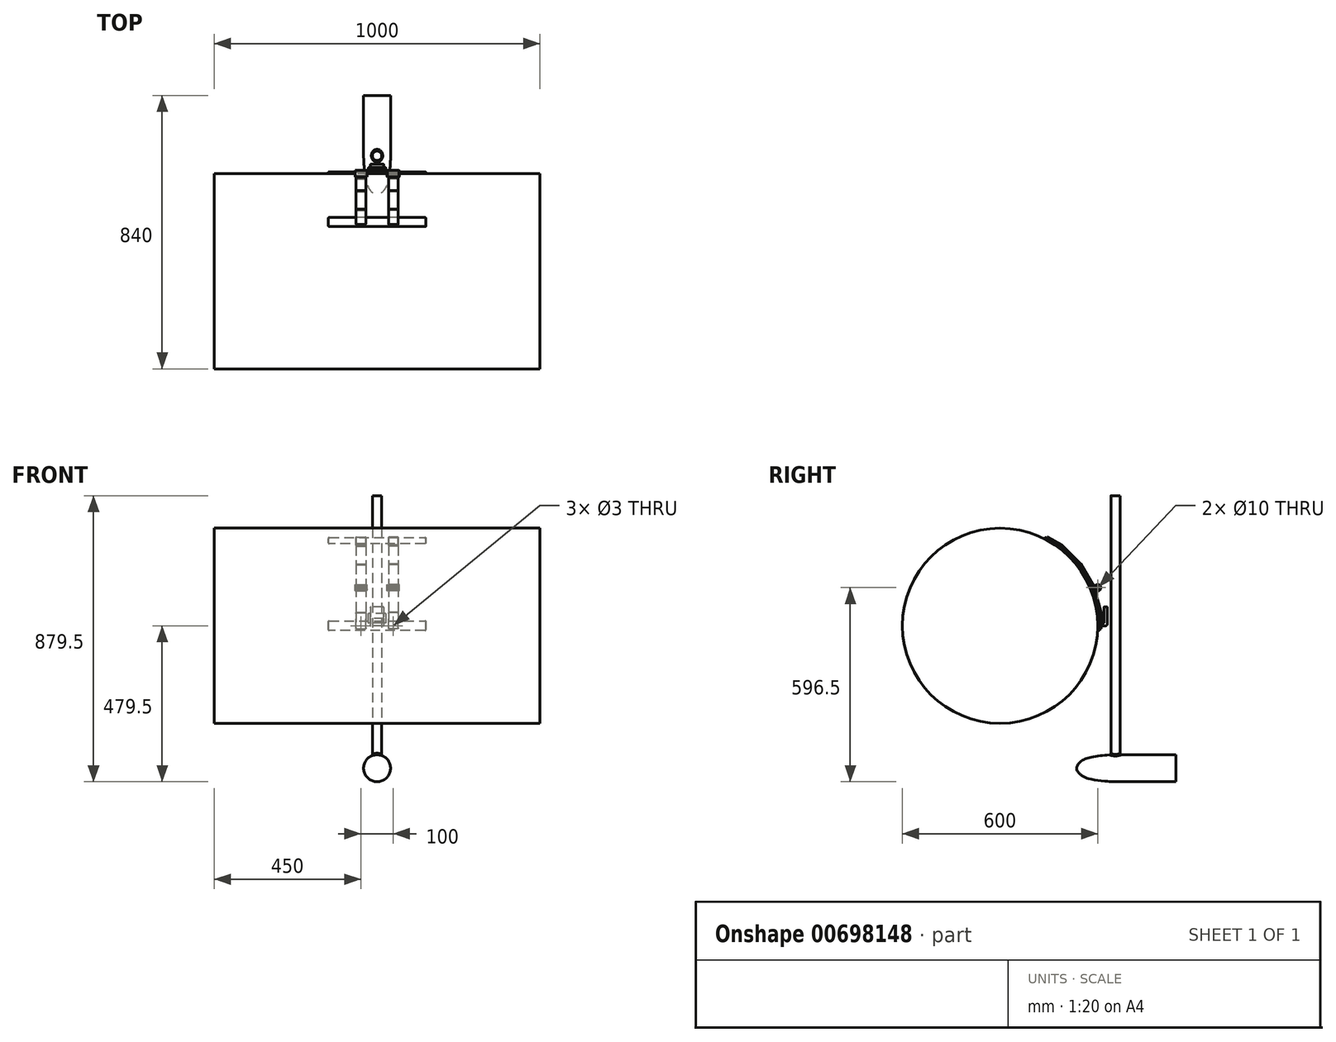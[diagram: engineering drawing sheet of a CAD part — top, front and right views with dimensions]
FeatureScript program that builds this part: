
annotation { "Feature Type Name" : "Feature", "Feature Type Description" : "" }
export const myFeature = defineFeature(function(context is Context, id is Id, definition is map)
    precondition{}
    {
        {
            var Q0;
            Q0=qCreatedBy(makeId("Right.planeOp"),FACE);
            var sketch = newSketch(context, id + "F0", { "sketchPlane" : qUnion([Q0])});
            skCircle(sketch, "E0", {"center": v(0, 0) * mm, "radius": 300 * mm});
            skSolve(sketch);
        }
        {
            var Q0;
            Q0=makeQuery(id+"F0.imprint","IMPRINT",FACE,{"disambiguationData":[TD([[makeQuery(id+"F0.imprint","IMPRINT",EDGE,{"derivedFrom":sQuery(id+"F0.wireOp",EDGE,"E0")}),1.0]])]});
            extrude(context, id + "F1", {"entities" : qUnion([Q0]), "endBound" : BoundingType.SYMMETRIC, "depth" : 1000 * mm, "offsetDistance" : 25 * mm});
        }
        {
            var Q0;
            Q0=qCreatedBy(makeId("Top.planeOp"),FACE);
            var sketch = newSketch(context, id + "F2", { "sketchPlane" : qUnion([Q0])});
            skLineSegment(sketch, "E1", {"start": v(0, 0) * mm, "end": v(0, 431.37) * mm, "construction": true});
            skCircle(sketch, "E2", {"center": v(0, 355) * mm, "radius": 14.5 * mm});
            skSolve(sketch);
        }
        {
            var Q0;
            Q0=makeQuery(id+"F2.imprint","IMPRINT",FACE,{"disambiguationData":[TD([[makeQuery(id+"F2.imprint","IMPRINT",EDGE,{"derivedFrom":sQuery(id+"F2.wireOp",EDGE,"E2")}),1.0]])]});
            extrude(context, id + "F3", {"entities" : qUnion([Q0]), "endBound" : BoundingType.SYMMETRIC, "depth" : 800 * mm, "offsetDistance" : 25 * mm});
        }
        {
            var Q0;
            Q0=qCreatedBy(makeId("Right.planeOp"),FACE);
            var sketch = newSketch(context, id + "F4", { "sketchPlane" : qUnion([Q0])});
            skLineSegment(sketch, "E3", {"start": v(235, -396.5) * mm, "end": v(384.53, -396.5) * mm, "construction": true});
            skLineSegment(sketch, "E4", {"start": v(355, -389.88) * mm, "end": v(355, -511.75) * mm, "construction": true});
            skFitSpline(sketch, "E5", {"points": [v(355, -396.5) * mm, v(273.73, -405.4) * mm, v(244.54, -420.82) * mm, v(235.02, -438) * mm], "startDerivative": vector(-142.28, 0) * mm, "endDerivative": vector(-0.8, -75.3) * mm});
            skLineSegment(sketch, "E6", {"start": v(355, -396.5) * mm, "end": v(540, -396.5) * mm});
            skLineSegment(sketch, "E7", {"start": v(540, -396.5) * mm, "end": v(540, -438) * mm});
            skLineSegment(sketch, "E8", {"start": v(235.02, -438) * mm, "end": v(540, -438) * mm});
            skSolve(sketch);
        }
        {
            var Q0;
            Q0 = qSketchRegion(id + "F4", true);
            var Q1;
            Q1=sQuery(id+"F4.wireOp",EDGE,"E8");
            revolve(context, id + "F5", {"surfaceOperationType" : NewSurfaceOperationType.NEW, "entities" : qUnion([Q0]), "axis" : qUnion([Q1]), "revolveType" : RevolveType.FULL});
        }
        {
            var Q0;
            Q0=sQuery(id+"F0.wireOp",EDGE,"E0");
            extrude(context, id + "F6", {"bodyType" : ToolBodyType.SURFACE, "surfaceEntities" : qUnion([Q0]), "endBound" : BoundingType.SYMMETRIC, "depth" : 1000 * mm, "offsetDistance" : 25 * mm});
        }
        {
            var Q0;
            Q0=makeQuery(id+"F3.opExtrude","SWEPT_BODY",BODY,{"disambiguationData":[OSD([sQuery(id+"F2.wireOp",EDGE,"E2")])]});
            var Q1;
            Q1=makeQuery(id+"F5.opRevolve","SWEPT_BODY",BODY,{"disambiguationData":[OSD([sQuery(id+"F4.wireOp",EDGE,"E5"),sQuery(id+"F4.wireOp",EDGE,"E6"),sQuery(id+"F4.wireOp",EDGE,"E7"),sQuery(id+"F4.wireOp",EDGE,"iDBx6k7e-QWYk-5wCq-wD4t-SSnstJS5jygN")])]});
            booleanBodies(context, id + "F7", {"operationType" : BooleanOperationType.UNION, "tools" : qUnion([Q0, Q1])});
        }
        {
            var Q0;
            Q0=makeQuery(id+"F7.opBoolean","INTERSECT",EDGE,{"derivedFrom":[makeQuery(id+"F3.opExtrude","SWEPT_FACE",FACE,{"disambiguationData":[OSD([sQuery(id+"F2.wireOp",EDGE,"E2")])]}),makeQuery(id+"F5.opRevolve","SWEPT_FACE",FACE,{"disambiguationData":[OSD([sQuery(id+"F4.wireOp",EDGE,"E6")])]})]});
            fillet(context, id + "F8", {"entities" : qUnion([Q0]), "radius" : 5 * mm, "tangentPropagation" : true, "allowEdgeOverflow" : false});
        }
        {
            var Q0;
            Q0=qCreatedBy(makeId("Right.planeOp"),FACE);
            cPlane(context, id + "F9", {"entities" : qUnion([Q0]), "cplaneType" : CPlaneType.OFFSET, "offset" : 35 * mm, "width" : 150 * mm, "height" : 150 * mm});
        }
        {
            var Q0;
            Q0=qCreatedBy(makeId("Right.planeOp"),FACE);
            var sketch = newSketch(context, id + "F10", { "sketchPlane" : qUnion([Q0])});
            skLineSegment(sketch, "E9", {"start": v(0, 0) * mm, "end": v(152.5, 264.14) * mm, "construction": true});
            skLineSegment(sketch, "E10", {"start": v(152.5, 264.14) * mm, "end": v(165.5, 256.64) * mm});
            skLineSegment(sketch, "E11", {"start": v(163, 252.3) * mm, "end": v(137, 267.3) * mm});
            skLineSegment(sketch, "E12", {"start": v(152.5, 264.14) * mm, "end": v(139.42, 271.7) * mm});
            skLineSegment(sketch, "E13", {"start": v(139.42, 271.7) * mm, "end": v(137, 267.3) * mm});
            skLineSegment(sketch, "E14", {"start": v(165.5, 256.64) * mm, "end": v(163, 252.3) * mm});
            skSolve(sketch);
        }
        {
            var Q0;
            Q0 = qSketchRegion(id + "F10", true);
            extrude(context, id + "F11", {"entities" : qUnion([Q0]), "endBound" : BoundingType.SYMMETRIC, "depth" : 300 * mm, "offsetDistance" : 25 * mm});
        }
        {
            var Q0;
            Q0=makeQuery(id+"F11.opExtrude","CAP_EDGE",EDGE,{"disambiguationData":[OSD([sQuery(id+"F10.wireOp",EDGE,"E11")])],"isStart":false});
            var Q1;
            Q1=makeQuery(id+"F11.opExtrude","CAP_EDGE",EDGE,{"disambiguationData":[OSD([sQuery(id+"F10.wireOp",EDGE,"E10"),sQuery(id+"F10.wireOp",EDGE,"E12")])],"isStart":false});
            var Q2;
            Q2=makeQuery(id+"F11.opExtrude","SWEPT_EDGE",EDGE,{"disambiguationData":[OSD([sQuery(id+"F10.wireOp",EDGE,"E11"),sQuery(id+"F10.wireOp",EDGE,"E13")])]});
            var Q3;
            Q3=makeQuery(id+"F11.opExtrude","SWEPT_EDGE",EDGE,{"disambiguationData":[OSD([sQuery(id+"F10.wireOp",EDGE,"E12"),sQuery(id+"F10.wireOp",EDGE,"E13")])]});
            var Q4;
            Q4=makeQuery(id+"F11.opExtrude","CAP_EDGE",EDGE,{"disambiguationData":[OSD([sQuery(id+"F10.wireOp",EDGE,"E11")])],"isStart":true});
            var Q5;
            Q5=makeQuery(id+"F11.opExtrude","CAP_EDGE",EDGE,{"disambiguationData":[OSD([sQuery(id+"F10.wireOp",EDGE,"E10"),sQuery(id+"F10.wireOp",EDGE,"E12")])],"isStart":true});
            var Q6;
            Q6=makeQuery(id+"F11.opExtrude","SWEPT_EDGE",EDGE,{"disambiguationData":[OSD([sQuery(id+"F10.wireOp",EDGE,"E11"),sQuery(id+"F10.wireOp",EDGE,"E14")])]});
            var Q7;
            Q7=makeQuery(id+"F11.opExtrude","SWEPT_EDGE",EDGE,{"disambiguationData":[OSD([sQuery(id+"F10.wireOp",EDGE,"E10"),sQuery(id+"F10.wireOp",EDGE,"E14")])]});
            fillet(context, id + "F12", {"entities" : qUnion([Q0, Q1, Q2, Q3, Q4, Q5, Q6, Q7]), "tangentPropagation" : true, "radius" : 1 * mm, "defaultsChanged" : false, "vertexSettings" : [], "allowEdgeOverflow" : false});
        }
        {
            var Q0;
            Q0=makeQuery(id+"F11.opExtrude","CAP_EDGE",EDGE,{"disambiguationData":[OSD([sQuery(id+"F10.wireOp",EDGE,"E13")])],"isStart":false});
            var Q1;
            Q1=makeQuery(id+"F11.opExtrude","CAP_EDGE",EDGE,{"disambiguationData":[OSD([sQuery(id+"F10.wireOp",EDGE,"E14")])],"isStart":false});
            var Q2;
            Q2=makeQuery(id+"F11.opExtrude","CAP_EDGE",EDGE,{"disambiguationData":[OSD([sQuery(id+"F10.wireOp",EDGE,"E14")])],"isStart":true});
            var Q3;
            Q3=makeQuery(id+"F11.opExtrude","CAP_EDGE",EDGE,{"disambiguationData":[OSD([sQuery(id+"F10.wireOp",EDGE,"E13")])],"isStart":true});
            fillet(context, id + "F13", {"entities" : qUnion([Q0, Q1, Q2, Q3]), "tangentPropagation" : true, "radius" : 3 * mm, "defaultsChanged" : true, "vertexSettings" : [], "allowEdgeOverflow" : false});
        }
        {
            var Q0;
            Q0=makeQuery(id+"F11.opExtrude","SWEPT_BODY",BODY,{"disambiguationData":[OSD([sQuery(id+"F10.wireOp",EDGE,"E10"),sQuery(id+"F10.wireOp",EDGE,"E11"),sQuery(id+"F10.wireOp",EDGE,"E12"),sQuery(id+"F10.wireOp",EDGE,"E13"),sQuery(id+"F10.wireOp",EDGE,"E14")])]});
            var Q1;
            Q1=makeQuery(id+"F1.opExtrude","SWEPT_FACE",FACE,{"disambiguationData":[OSD([sQuery(id+"F0.wireOp",EDGE,"E0")])]});
            transform(context, id + "F14", {"entities" : qUnion([Q0]), "transformType" : TransformType.ROTATION, "transformAxis" : qUnion([Q1]), "angle" : 60 * degree, "makeCopy" : true});
        }
        {
            var Q0;
            Q0=qCreatedBy(id+"F9.planeOp",FACE);
            var sketch = newSketch(context, id + "F15", { "sketchPlane" : qUnion([Q0])});
            skLineSegment(sketch, "E15", {"start": v(0, 0) * mm, "end": v(165.42, 286.52) * mm, "construction": true});
            skLineSegment(sketch, "E16", {"start": v(0, 0) * mm, "end": v(327, 0) * mm, "construction": true});
            skLineSegment(sketch, "E17", {"start": v(0, 0) * mm, "end": v(202.83, 264.33) * mm, "construction": true});
            skLineSegment(sketch, "E18", {"start": v(0, 0) * mm, "end": v(263.06, 201.85) * mm, "construction": true});
            skLineSegment(sketch, "E19", {"start": v(0, 0) * mm, "end": v(296.71, 122.9) * mm, "construction": true});
            skLineSegment(sketch, "E20", {"start": v(0, 0) * mm, "end": v(324.75, 42.75) * mm, "construction": true});
            skLineSegment(sketch, "E21", {"start": v(143.84, 269.14) * mm, "end": v(187.27, 244.06) * mm});
            skLineSegment(sketch, "E22", {"start": v(190.34, 248.06) * mm, "end": v(146.34, 273.47) * mm});
            skLineSegment(sketch, "E23", {"start": v(146.34, 273.47) * mm, "end": v(143.84, 269.14) * mm});
            skArc(sketch, "E24", {"start": v(187.27, 244.06) * mm, "mid": v(266.42, 153.82) * mm, "end": v(305, 40.15) * mm, "construction": true});
            skLineSegment(sketch, "E25", {"start": v(187.27, 244.06) * mm, "end": v(244.06, 187.27) * mm});
            skLineSegment(sketch, "E26", {"start": v(244.06, 187.27) * mm, "end": v(284.21, 117.73) * mm});
            skLineSegment(sketch, "E27", {"start": v(284.21, 117.73) * mm, "end": v(305, 40.15) * mm});
            skLineSegment(sketch, "E28", {"start": v(305, -10) * mm, "end": v(310, -10) * mm});
            skLineSegment(sketch, "E29", {"start": v(305, 40.15) * mm, "end": v(305, -10) * mm});
            skLineSegment(sketch, "E30", {"start": v(310, -10) * mm, "end": v(310, 40.81) * mm});
            skLineSegment(sketch, "E31", {"start": v(190.34, 248.06) * mm, "end": v(248.06, 190.34) * mm});
            skLineSegment(sketch, "E32", {"start": v(248.06, 190.34) * mm, "end": v(288.87, 119.66) * mm});
            skLineSegment(sketch, "E33", {"start": v(288.87, 119.66) * mm, "end": v(310, 40.81) * mm});
            skSolve(sketch);
        }
        {
            var Q0;
            Q0 = qSketchRegion(id + "F15", true);
            extrude(context, id + "F16", {"entities" : qUnion([Q0]), "depth" : 30 * mm, "offsetDistance" : 25 * mm, "hasSecondDirection" : true, "secondDirectionOppositeDirection" : false, "secondDirectionDepth" : 0 * mm});
        }
        {
            var Q0;
            Q0=makeQuery(id+"F16.opExtrude","CAP_EDGE",EDGE,{"disambiguationData":[OSD([sQuery(id+"F15.wireOp",EDGE,"E22")])],"isStart":false});
            var Q1;
            Q1=makeQuery(id+"F16.opExtrude","CAP_EDGE",EDGE,{"disambiguationData":[OSD([sQuery(id+"F15.wireOp",EDGE,"E21")])],"isStart":false});
            var Q2;
            Q2=makeQuery(id+"F16.opExtrude","CAP_EDGE",EDGE,{"disambiguationData":[OSD([sQuery(id+"F15.wireOp",EDGE,"E22")])],"isStart":true});
            var Q3;
            Q3=makeQuery(id+"F16.opExtrude","CAP_EDGE",EDGE,{"disambiguationData":[OSD([sQuery(id+"F15.wireOp",EDGE,"E21")])],"isStart":true});
            var Q4;
            Q4=makeQuery(id+"F16.opExtrude","CAP_EDGE",EDGE,{"disambiguationData":[OSD([sQuery(id+"F15.wireOp",EDGE,"E31")])],"isStart":false});
            var Q5;
            Q5=makeQuery(id+"F16.opExtrude","CAP_EDGE",EDGE,{"disambiguationData":[OSD([sQuery(id+"F15.wireOp",EDGE,"E32")])],"isStart":false});
            var Q6;
            Q6=makeQuery(id+"F16.opExtrude","CAP_EDGE",EDGE,{"disambiguationData":[OSD([sQuery(id+"F15.wireOp",EDGE,"E33")])],"isStart":false});
            var Q7;
            Q7=makeQuery(id+"F16.opExtrude","CAP_EDGE",EDGE,{"disambiguationData":[OSD([sQuery(id+"F15.wireOp",EDGE,"E27")])],"isStart":false});
            var Q8;
            Q8=makeQuery(id+"F16.opExtrude","CAP_EDGE",EDGE,{"disambiguationData":[OSD([sQuery(id+"F15.wireOp",EDGE,"E30")])],"isStart":false});
            var Q9;
            Q9=makeQuery(id+"F16.opExtrude","CAP_EDGE",EDGE,{"disambiguationData":[OSD([sQuery(id+"F15.wireOp",EDGE,"E29")])],"isStart":false});
            var Q10;
            Q10=makeQuery(id+"F16.opExtrude","SWEPT_EDGE",EDGE,{"disambiguationData":[OSD([sQuery(id+"F15.wireOp",EDGE,"E28"),sQuery(id+"F15.wireOp",EDGE,"E30")])]});
            var Q11;
            Q11=makeQuery(id+"F16.opExtrude","SWEPT_EDGE",EDGE,{"disambiguationData":[OSD([sQuery(id+"F15.wireOp",EDGE,"E28"),sQuery(id+"F15.wireOp",EDGE,"E29")])]});
            var Q12;
            Q12=makeQuery(id+"F16.opExtrude","CAP_EDGE",EDGE,{"disambiguationData":[OSD([sQuery(id+"F15.wireOp",EDGE,"E30")])],"isStart":true});
            var Q13;
            Q13=makeQuery(id+"F16.opExtrude","CAP_EDGE",EDGE,{"disambiguationData":[OSD([sQuery(id+"F15.wireOp",EDGE,"E29")])],"isStart":true});
            var Q14;
            Q14=makeQuery(id+"F16.opExtrude","CAP_EDGE",EDGE,{"disambiguationData":[OSD([sQuery(id+"F15.wireOp",EDGE,"E33")])],"isStart":true});
            var Q15;
            Q15=makeQuery(id+"F16.opExtrude","CAP_EDGE",EDGE,{"disambiguationData":[OSD([sQuery(id+"F15.wireOp",EDGE,"E27")])],"isStart":true});
            var Q16;
            Q16=makeQuery(id+"F16.opExtrude","CAP_EDGE",EDGE,{"disambiguationData":[OSD([sQuery(id+"F15.wireOp",EDGE,"E32")])],"isStart":true});
            var Q17;
            Q17=makeQuery(id+"F16.opExtrude","CAP_EDGE",EDGE,{"disambiguationData":[OSD([sQuery(id+"F15.wireOp",EDGE,"E31")])],"isStart":true});
            var Q18;
            Q18=makeQuery(id+"F16.opExtrude","CAP_EDGE",EDGE,{"disambiguationData":[OSD([sQuery(id+"F15.wireOp",EDGE,"E26")])],"isStart":true});
            var Q19;
            Q19=makeQuery(id+"F16.opExtrude","CAP_EDGE",EDGE,{"disambiguationData":[OSD([sQuery(id+"F15.wireOp",EDGE,"E25")])],"isStart":true});
            var Q20;
            Q20=makeQuery(id+"F16.opExtrude","SWEPT_EDGE",EDGE,{"disambiguationData":[OSD([sQuery(id+"F15.wireOp",EDGE,"E22"),sQuery(id+"F15.wireOp",EDGE,"E23")])]});
            var Q21;
            Q21=makeQuery(id+"F16.opExtrude","CAP_EDGE",EDGE,{"disambiguationData":[OSD([sQuery(id+"F15.wireOp",EDGE,"E26")])],"isStart":false});
            var Q22;
            Q22=makeQuery(id+"F16.opExtrude","CAP_EDGE",EDGE,{"disambiguationData":[OSD([sQuery(id+"F15.wireOp",EDGE,"E25")])],"isStart":false});
            var Q23;
            Q23=makeQuery(id+"F16.opExtrude","SWEPT_EDGE",EDGE,{"disambiguationData":[OSD([sQuery(id+"F15.wireOp",EDGE,"E21"),sQuery(id+"F15.wireOp",EDGE,"E23")])]});
            var Q24;
            Q24=makeQuery(id+"F16.opExtrude","CAP_EDGE",EDGE,{"disambiguationData":[OSD([sQuery(id+"F15.wireOp",EDGE,"E23")])],"isStart":true});
            var Q25;
            Q25=makeQuery(id+"F16.opExtrude","CAP_EDGE",EDGE,{"disambiguationData":[OSD([sQuery(id+"F15.wireOp",EDGE,"E23")])],"isStart":false});
            var Q26;
            Q26=makeQuery(id+"F16.opExtrude","CAP_EDGE",EDGE,{"disambiguationData":[OSD([sQuery(id+"F15.wireOp",EDGE,"E28")])],"isStart":true});
            var Q27;
            Q27=makeQuery(id+"F16.opExtrude","CAP_EDGE",EDGE,{"disambiguationData":[OSD([sQuery(id+"F15.wireOp",EDGE,"E28")])],"isStart":false});
            fillet(context, id + "F17", {"entities" : qUnion([Q0, Q1, Q2, Q3, Q4, Q5, Q6, Q7, Q8, Q9, Q10, Q11, Q12, Q13, Q14, Q15, Q16, Q17, Q18, Q19, Q20, Q21, Q22, Q23, Q24, Q25, Q26, Q27]), "tangentPropagation" : true, "radius" : 1 * mm, "defaultsChanged" : false, "vertexSettings" : [], "allowEdgeOverflow" : false});
        }
        {
            var Q0;
            Q0=qCreatedBy(makeId("Right.planeOp"),FACE);
            var sketch = newSketch(context, id + "F18", { "sketchPlane" : qUnion([Q0])});
            skCircle(sketch, "E34", {"center": v(300, 117) * mm, "radius": 10 * mm});
            skCircle(sketch, "E35", {"center": v(300, 117) * mm, "radius": 5 * mm});
            skLineSegment(sketch, "E36", {"start": v(311, 8) * mm, "end": v(319, 8) * mm});
            skLineSegment(sketch, "E37", {"start": v(319, 8) * mm, "end": v(319, 38) * mm});
            skLineSegment(sketch, "E38", {"start": v(319, 38) * mm, "end": v(311, 38) * mm});
            skLineSegment(sketch, "E39", {"start": v(311, 38) * mm, "end": v(311, 8) * mm});
            skSolve(sketch);
        }
        {
            var Q0;
            Q0=makeQuery(id+"F18.imprint","IMPRINT",FACE,{"disambiguationData":[TD([[makeQuery(id+"F18.imprint","IMPRINT",EDGE,{"derivedFrom":sQuery(id+"F18.wireOp",EDGE,"E34")}),1.0]])]});
            extrude(context, id + "F19", {"entities" : qUnion([Q0]), "depth" : 68 * mm, "offsetDistance" : 25 * mm, "hasSecondDirection" : true, "secondDirectionOppositeDirection" : false, "secondDirectionDepth" : 30 * mm});
        }
        {
            var Q0;
            Q0=makeQuery(id+"F19.opExtrude","CAP_EDGE",EDGE,{"disambiguationData":[OSD([sQuery(id+"F18.wireOp",EDGE,"E35")])],"isStart":false});
            var Q1;
            Q1=makeQuery(id+"F19.opExtrude","CAP_EDGE",EDGE,{"disambiguationData":[OSD([sQuery(id+"F18.wireOp",EDGE,"E34")])],"isStart":false});
            var Q2;
            Q2=makeQuery(id+"F19.opExtrude","CAP_EDGE",EDGE,{"disambiguationData":[OSD([sQuery(id+"F18.wireOp",EDGE,"E34")])],"isStart":true});
            var Q3;
            Q3=makeQuery(id+"F19.opExtrude","CAP_EDGE",EDGE,{"disambiguationData":[OSD([sQuery(id+"F18.wireOp",EDGE,"E35")])],"isStart":true});
            chamfer(context, id + "F20", {"entities" : qUnion([Q0, Q1, Q2, Q3]), "width" : 1 * mm, "tangentPropagation" : true});
        }
        {
            var Q0;
            Q0=makeQuery(id+"F18.imprint","IMPRINT",FACE,{"disambiguationData":[TD([[makeQuery(id+"F18.imprint","IMPRINT",EDGE,{"derivedFrom":sQuery(id+"F18.wireOp",EDGE,"E36")}),1.0]])]});
            extrude(context, id + "F21", {"entities" : qUnion([Q0]), "endBound" : BoundingType.SYMMETRIC, "depth" : 54 * mm, "offsetDistance" : 25 * mm});
        }
        {
            var Q0;
            Q0=makeQuery(id+"F21.opExtrude","CAP_EDGE",EDGE,{"disambiguationData":[OSD([sQuery(id+"F18.wireOp",EDGE,"E37")])],"isStart":false});
            var Q1;
            Q1=makeQuery(id+"F21.opExtrude","SWEPT_EDGE",EDGE,{"disambiguationData":[OSD([sQuery(id+"F18.wireOp",EDGE,"E36"),sQuery(id+"F18.wireOp",EDGE,"E37")])]});
            var Q2;
            Q2=makeQuery(id+"F21.opExtrude","CAP_EDGE",EDGE,{"disambiguationData":[OSD([sQuery(id+"F18.wireOp",EDGE,"E39")])],"isStart":true});
            var Q3;
            Q3=makeQuery(id+"F21.opExtrude","SWEPT_EDGE",EDGE,{"disambiguationData":[OSD([sQuery(id+"F18.wireOp",EDGE,"E37"),sQuery(id+"F18.wireOp",EDGE,"E38")])]});
            var Q4;
            Q4=makeQuery(id+"F21.opExtrude","CAP_EDGE",EDGE,{"disambiguationData":[OSD([sQuery(id+"F18.wireOp",EDGE,"E37")])],"isStart":true});
            var Q5;
            Q5=makeQuery(id+"F21.opExtrude","SWEPT_EDGE",EDGE,{"disambiguationData":[OSD([sQuery(id+"F18.wireOp",EDGE,"E38"),sQuery(id+"F18.wireOp",EDGE,"E39")])]});
            var Q6;
            Q6=makeQuery(id+"F21.opExtrude","SWEPT_EDGE",EDGE,{"disambiguationData":[OSD([sQuery(id+"F18.wireOp",EDGE,"E36"),sQuery(id+"F18.wireOp",EDGE,"E39")])]});
            var Q7;
            Q7=makeQuery(id+"F21.opExtrude","CAP_EDGE",EDGE,{"disambiguationData":[OSD([sQuery(id+"F18.wireOp",EDGE,"E39")])],"isStart":false});
            var Q8;
            Q8=makeQuery(id+"F21.opExtrude","CAP_EDGE",EDGE,{"disambiguationData":[OSD([sQuery(id+"F18.wireOp",EDGE,"E36")])],"isStart":false});
            var Q9;
            Q9=makeQuery(id+"F21.opExtrude","CAP_EDGE",EDGE,{"disambiguationData":[OSD([sQuery(id+"F18.wireOp",EDGE,"E36")])],"isStart":true});
            var Q10;
            Q10=makeQuery(id+"F21.opExtrude","CAP_EDGE",EDGE,{"disambiguationData":[OSD([sQuery(id+"F18.wireOp",EDGE,"E38")])],"isStart":false});
            var Q11;
            Q11=makeQuery(id+"F21.opExtrude","CAP_EDGE",EDGE,{"disambiguationData":[OSD([sQuery(id+"F18.wireOp",EDGE,"E38")])],"isStart":true});
            fillet(context, id + "F22", {"entities" : qUnion([Q0, Q1, Q2, Q3, Q4, Q5, Q6, Q7, Q8, Q9, Q10, Q11]), "tangentPropagation" : true, "radius" : 1 * mm, "defaultsChanged" : false, "vertexSettings" : [], "allowEdgeOverflow" : false});
        }
        {
            var Q0;
            Q0=makeQuery(id+"F16.opExtrude","SWEPT_FACE",FACE,{"disambiguationData":[OSD([sQuery(id+"F15.wireOp",EDGE,"E30")])]});
            var sketch = newSketch(context, id + "F23", { "sketchPlane" : qUnion([Q0])});
            skPoint(sketch, "E40.0", {"position": v(-50, -10) * mm});
            skCircle(sketch, "E41", {"center": v(-50, 0) * mm, "radius": 1.5 * mm});
            skSolve(sketch);
        }
        {
            var Q0;
            Q0 = qSketchRegion(id + "F23", true);
            extrude(context, id + "F24", {"entities" : qUnion([Q0]), "operationType" : NewBodyOperationType.REMOVE, "oppositeDirection" : true, "depth" : 10 * mm, "offsetDistance" : 25 * mm});
        }
        {
            var Q0;
            Q0=qCreatedBy(makeId("Right.planeOp"),FACE);
            var sketch = newSketch(context, id + "F25", { "sketchPlane" : qUnion([Q0])});
            skLineSegment(sketch, "E42", {"start": v(305, 22) * mm, "end": v(311, 22) * mm});
            skLineSegment(sketch, "E43", {"start": v(311, 22) * mm, "end": v(311, 8) * mm});
            skLineSegment(sketch, "E44", {"start": v(311, 8) * mm, "end": v(319, 8) * mm});
            skLineSegment(sketch, "E45", {"start": v(319, 8) * mm, "end": v(319, 58) * mm});
            skLineSegment(sketch, "E46", {"start": v(319, 58) * mm, "end": v(329, 58) * mm});
            skLineSegment(sketch, "E47", {"start": v(329, 58) * mm, "end": v(329, 0) * mm});
            skLineSegment(sketch, "E48", {"start": v(329, 0) * mm, "end": v(305, 0) * mm});
            skLineSegment(sketch, "E49", {"start": v(305, 22) * mm, "end": v(305, 0) * mm});
            skSolve(sketch);
        }
        {
            var Q0;
            Q0 = qSketchRegion(id + "F25", true);
            extrude(context, id + "F26", {"entities" : qUnion([Q0]), "endBound" : BoundingType.SYMMETRIC, "depth" : 41 * mm, "offsetDistance" : 25 * mm});
        }
        {
            var Q0;
            Q0=makeQuery(id+"F26.opExtrude","SWEPT_EDGE",EDGE,{"disambiguationData":[OSD([sQuery(id+"F25.wireOp",EDGE,"E47"),sQuery(id+"F25.wireOp",EDGE,"E48")])]});
            var Q1;
            Q1=makeQuery(id+"F26.opExtrude","SWEPT_EDGE",EDGE,{"disambiguationData":[OSD([sQuery(id+"F25.wireOp",EDGE,"E48"),sQuery(id+"F25.wireOp",EDGE,"E49")])]});
            fillet(context, id + "F27", {"entities" : qUnion([Q0, Q1]), "tangentPropagation" : true, "radius" : 4 * mm, "defaultsChanged" : true, "vertexSettings" : [], "allowEdgeOverflow" : false});
        }
        {
            var Q0;
            Q0=makeQuery(id+"F26.opExtrude","SWEPT_EDGE",EDGE,{"disambiguationData":[OSD([sQuery(id+"F25.wireOp",EDGE,"E43"),sQuery(id+"F25.wireOp",EDGE,"E44")])]});
            var Q1;
            Q1=makeQuery(id+"F26.opExtrude","SWEPT_EDGE",EDGE,{"disambiguationData":[OSD([sQuery(id+"F25.wireOp",EDGE,"E44"),sQuery(id+"F25.wireOp",EDGE,"E45")])]});
            var Q2;
            Q2=makeQuery(id+"F26.opExtrude","SWEPT_EDGE",EDGE,{"disambiguationData":[OSD([sQuery(id+"F25.wireOp",EDGE,"E42"),sQuery(id+"F25.wireOp",EDGE,"E43")])]});
            var Q3;
            Q3=makeQuery(id+"F26.opExtrude","SWEPT_EDGE",EDGE,{"disambiguationData":[OSD([sQuery(id+"F25.wireOp",EDGE,"E42"),sQuery(id+"F25.wireOp",EDGE,"E49")])]});
            var Q4;
            Q4=makeQuery(id+"F26.opExtrude","SWEPT_EDGE",EDGE,{"disambiguationData":[OSD([sQuery(id+"F25.wireOp",EDGE,"E45"),sQuery(id+"F25.wireOp",EDGE,"E46")])]});
            var Q5;
            Q5=makeQuery(id+"F26.opExtrude","SWEPT_EDGE",EDGE,{"disambiguationData":[OSD([sQuery(id+"F25.wireOp",EDGE,"E46"),sQuery(id+"F25.wireOp",EDGE,"E47")])]});
            var Q6;
            Q6=makeQuery(id+"F26.opExtrude","CAP_EDGE",EDGE,{"disambiguationData":[OSD([sQuery(id+"F25.wireOp",EDGE,"E47")])],"isStart":false});
            var Q7;
            Q7=makeQuery(id+"F26.opExtrude","CAP_EDGE",EDGE,{"disambiguationData":[OSD([sQuery(id+"F25.wireOp",EDGE,"E47")])],"isStart":true});
            var Q8;
            Q8=makeQuery(id+"F26.opExtrude","CAP_EDGE",EDGE,{"disambiguationData":[OSD([sQuery(id+"F25.wireOp",EDGE,"E45")])],"isStart":false});
            var Q9;
            Q9=makeQuery(id+"F26.opExtrude","CAP_EDGE",EDGE,{"disambiguationData":[OSD([sQuery(id+"F25.wireOp",EDGE,"E46")])],"isStart":false});
            var Q10;
            Q10=makeQuery(id+"F26.opExtrude","CAP_EDGE",EDGE,{"disambiguationData":[OSD([sQuery(id+"F25.wireOp",EDGE,"E46")])],"isStart":true});
            var Q11;
            Q11=makeQuery(id+"F26.opExtrude","CAP_EDGE",EDGE,{"disambiguationData":[OSD([sQuery(id+"F25.wireOp",EDGE,"E45")])],"isStart":true});
            fillet(context, id + "F28", {"entities" : qUnion([Q0, Q1, Q2, Q3, Q4, Q5, Q6, Q7, Q8, Q9, Q10, Q11]), "tangentPropagation" : true, "radius" : 1 * mm, "defaultsChanged" : false, "vertexSettings" : [], "allowEdgeOverflow" : false});
        }
        {
            var Q0;
            Q0=makeQuery(id+"F16.opExtrude","SWEPT_BODY",BODY,{"disambiguationData":[OSD([sQuery(id+"F15.wireOp",EDGE,"E21"),sQuery(id+"F15.wireOp",EDGE,"E22"),sQuery(id+"F15.wireOp",EDGE,"E23"),sQuery(id+"F15.wireOp",EDGE,"E25"),sQuery(id+"F15.wireOp",EDGE,"E26"),sQuery(id+"F15.wireOp",EDGE,"E27"),sQuery(id+"F15.wireOp",EDGE,"E28"),sQuery(id+"F15.wireOp",EDGE,"E29"),sQuery(id+"F15.wireOp",EDGE,"E30"),sQuery(id+"F15.wireOp",EDGE,"E31"),sQuery(id+"F15.wireOp",EDGE,"E32"),sQuery(id+"F15.wireOp",EDGE,"E33")])]});
            var Q1;
            Q1=makeQuery(id+"F19.opExtrude","SWEPT_BODY",BODY,{"disambiguationData":[OSD([sQuery(id+"F18.wireOp",EDGE,"E34"),sQuery(id+"F18.wireOp",EDGE,"E35")])]});
            var Q2;
            Q2=qCreatedBy(makeId("Right.planeOp"),FACE);
            mirror(context, id + "F29", {"entities" : qUnion([Q0, Q1]), "mirrorPlane" : qUnion([Q2])});
        }
    });
